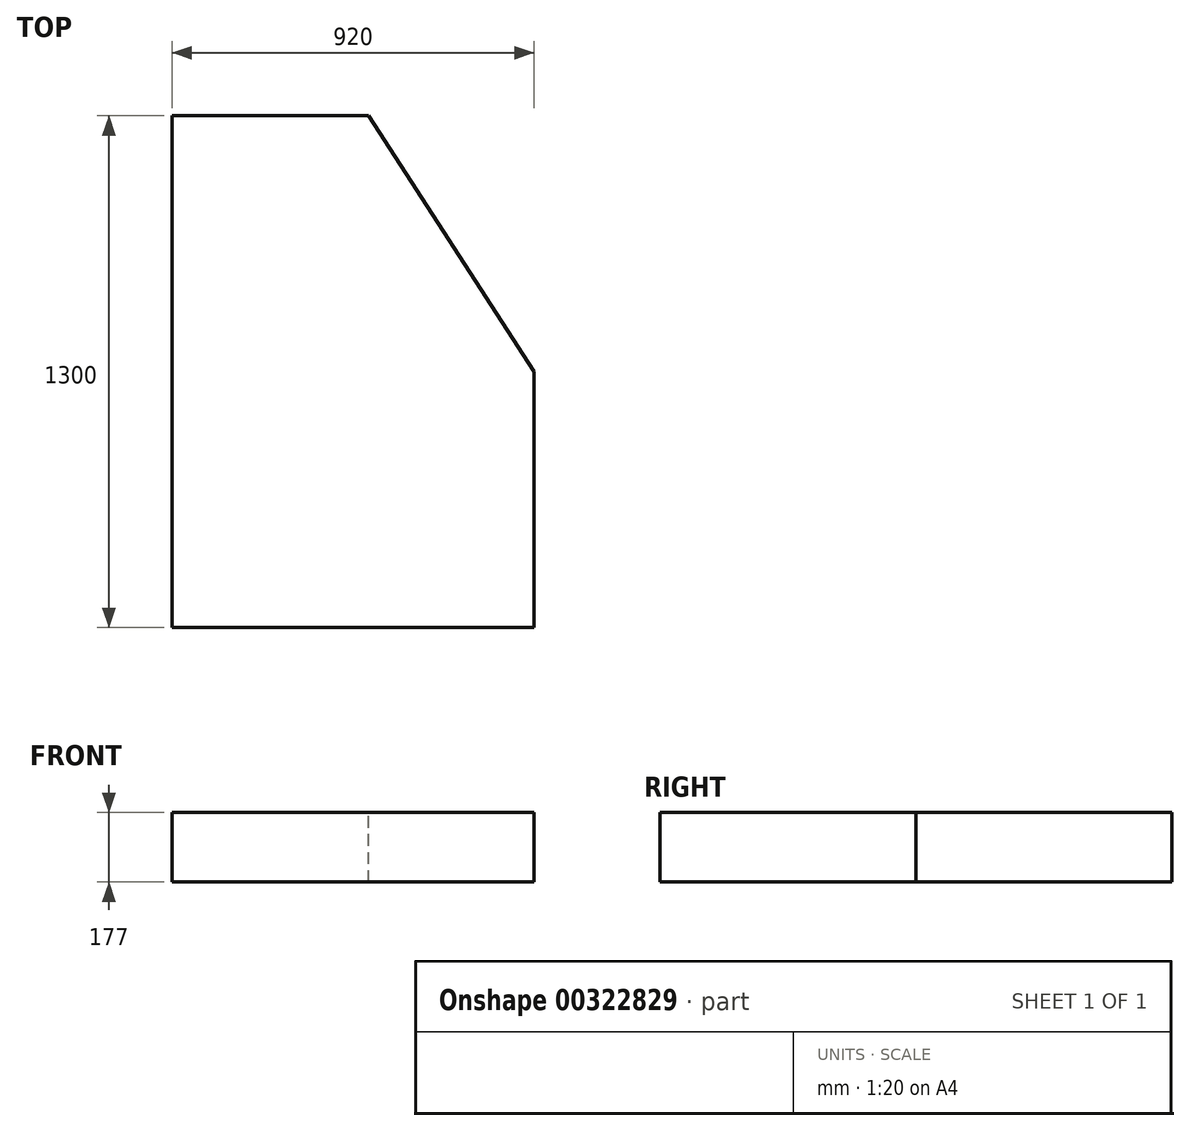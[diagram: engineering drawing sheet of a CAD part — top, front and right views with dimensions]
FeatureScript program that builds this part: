
annotation { "Feature Type Name" : "Feature", "Feature Type Description" : "" }
export const myFeature = defineFeature(function(context is Context, id is Id, definition is map)
    precondition{}
    {
        {
            var Q0;
            Q0=qCreatedBy(makeId("Top.planeOp"),FACE);
            var sketch = newSketch(context, id + "F0", { "sketchPlane" : qUnion([Q0])});
            skLineSegment(sketch, "E0.bottom", {"start": v(460, -650) * mm, "end": v(-460, -650) * mm});
            skLineSegment(sketch, "E0.right", {"start": v(-460, -650) * mm, "end": v(-460, 650) * mm});
            skPoint(sketch, "E0.middle", {"position": v(0, 0) * mm});
            skLineSegment(sketch, "E1", {"start": v(40, 650) * mm, "end": v(460, 0) * mm});
            skLineSegment(sketch, "E2", {"start": v(460, 0) * mm, "end": v(460, -650) * mm});
            skLineSegment(sketch, "E3", {"start": v(40, 650) * mm, "end": v(-460, 650) * mm});
            skSolve(sketch);
        }
        {
            var Q0;
            Q0=makeQuery(id+"F0.imprint","IMPRINT",FACE,{"disambiguationData":[TD([[makeQuery(id+"F0.imprint","IMPRINT",EDGE,{"derivedFrom":sQuery(id+"F0.wireOp",EDGE,"E0.bottom")}),-1.0]])]});
            extrude(context, id + "F1", {"entities" : qUnion([Q0]), "oppositeDirection" : true, "depth" : 177 * mm});
        }
    });
